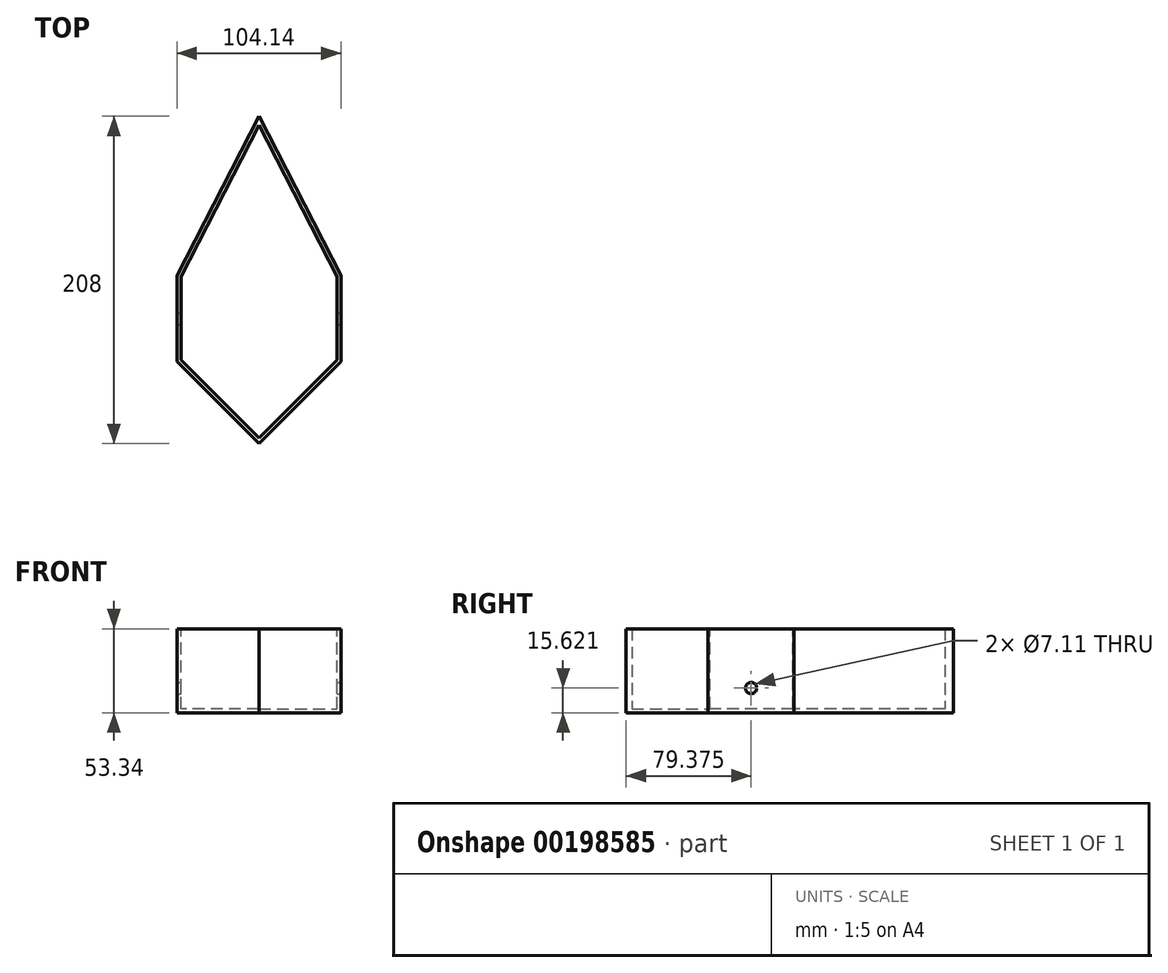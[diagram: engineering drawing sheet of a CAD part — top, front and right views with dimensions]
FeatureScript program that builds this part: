
annotation { "Feature Type Name" : "Feature", "Feature Type Description" : "" }
export const myFeature = defineFeature(function(context is Context, id is Id, definition is map)
    precondition{}
    {
        {
            var Q0;
            Q0=qCreatedBy(makeId("Top.planeOp"),FACE);
            var sketch = newSketch(context, id + "F0", { "sketchPlane" : qUnion([Q0])});
            skLineSegment(sketch, "E0.bottom", {"start": v(52.07, 104.14) * mm, "end": v(-52.07, 104.14) * mm});
            skLineSegment(sketch, "E0.top", {"start": v(52.07, -104.14) * mm, "end": v(-52.07, -104.14) * mm});
            skLineSegment(sketch, "E0.left", {"start": v(52.07, 104.14) * mm, "end": v(52.07, -104.14) * mm});
            skLineSegment(sketch, "E0.right", {"start": v(-52.07, 104.14) * mm, "end": v(-52.07, -104.14) * mm});
            skPoint(sketch, "E0.middle", {"position": v(0, 0) * mm});
            skSolve(sketch);
        }
        {
            var Q0;
            Q0=makeQuery(id+"F0.imprint","IMPRINT",FACE,{"disambiguationData":[TD([[makeQuery(id+"F0.imprint","IMPRINT",EDGE,{"derivedFrom":sQuery(id+"F0.wireOp",EDGE,"E0.bottom")}),1.0]])]});
            extrude(context, id + "F1", {"entities" : qUnion([Q0]), "depth" : 53.34 * mm});
        }
        {
            var Q0;
            Q0=makeQuery(id+"F1.opExtrude","SWEPT_EDGE",EDGE,{"disambiguationData":[OSD([sQuery(id+"F0.wireOp",EDGE,"E0.top"),sQuery(id+"F0.wireOp",EDGE,"E0.right")])]});
            var Q1;
            Q1=makeQuery(id+"F1.opExtrude","SWEPT_EDGE",EDGE,{"disambiguationData":[OSD([sQuery(id+"F0.wireOp",EDGE,"E0.top"),sQuery(id+"F0.wireOp",EDGE,"E0.left")])]});
            chamfer(context, id + "F2", {"entities" : qUnion([Q0, Q1]), "width" : 52.07 * mm, "tangentPropagation" : true});
        }
        {
            var Q0;
            Q0=makeQuery(id+"F1.opExtrude","SWEPT_EDGE",EDGE,{"disambiguationData":[OSD([sQuery(id+"F0.wireOp",EDGE,"E0.bottom"),sQuery(id+"F0.wireOp",EDGE,"E0.right")])]});
            var Q1;
            Q1=makeQuery(id+"F1.opExtrude","SWEPT_EDGE",EDGE,{"disambiguationData":[OSD([sQuery(id+"F0.wireOp",EDGE,"E0.bottom"),sQuery(id+"F0.wireOp",EDGE,"E0.left")])]});
            chamfer(context, id + "F3", {"entities" : qUnion([Q0, Q1]), "chamferType" : ChamferType.OFFSET_ANGLE, "width" : 101.6 * mm, "oppositeDirection" : false, "angle" : 27.2 * degree, "tangentPropagation" : true});
        }
        {
            var Q0;
            Q0=makeQuery(id+"F1.opExtrude","CAP_FACE",FACE,{"disambiguationData":[OSD([sQuery(id+"F0.wireOp",EDGE,"E0.bottom"),sQuery(id+"F0.wireOp",EDGE,"E0.top"),sQuery(id+"F0.wireOp",EDGE,"E0.left"),sQuery(id+"F0.wireOp",EDGE,"E0.right")])],"isStart":false});
            shell(context, id + "F4", {"entities" : qUnion([Q0]), "thickness" : 2.54 * mm});
        }
        {
            var Q0;
            Q0=makeQuery(id+"F1.opExtrude","SWEPT_FACE",FACE,{"disambiguationData":[OSD([sQuery(id+"F0.wireOp",EDGE,"E0.left")])]});
            var sketch = newSketch(context, id + "F5", { "sketchPlane" : qUnion([Q0])});
            skPoint(sketch, "E1", {"position": v(-24.76, 15.62) * mm});
            skPoint(sketch, "E2.orphan", {"position": v(-24.76, 53.34) * mm});
            skPoint(sketch, "E3.orphan", {"position": v(2.54, 15.62) * mm});
            skPoint(sketch, "E4.start.orphan", {"position": v(-24.76, 0) * mm});
            skPoint(sketch, "E5.end.orphan", {"position": v(-52.07, 15.62) * mm});
            skSolve(sketch);
        }
        {
            var Q0;
            Q0=sQuery(id+"F5.wireOp",VERTEX,"E1");
            var Q1;
            Q1=makeQuery(id+"F1.opExtrude","SWEPT_BODY",BODY,{"disambiguationData":[OSD([sQuery(id+"F0.wireOp",EDGE,"E0.bottom"),sQuery(id+"F0.wireOp",EDGE,"E0.top"),sQuery(id+"F0.wireOp",EDGE,"E0.left"),sQuery(id+"F0.wireOp",EDGE,"E0.right")])]});
            hole(context, id + "F6", {"style" : HoleStyle.SIMPLE, "endStyle" : HoleEndStyle.THROUGH, "holeDiameter" : 7.11 * mm, "locations" : qUnion([Q0]), "scope" : qUnion([Q1]), "isTappedThrough" : true});
        }
    });
